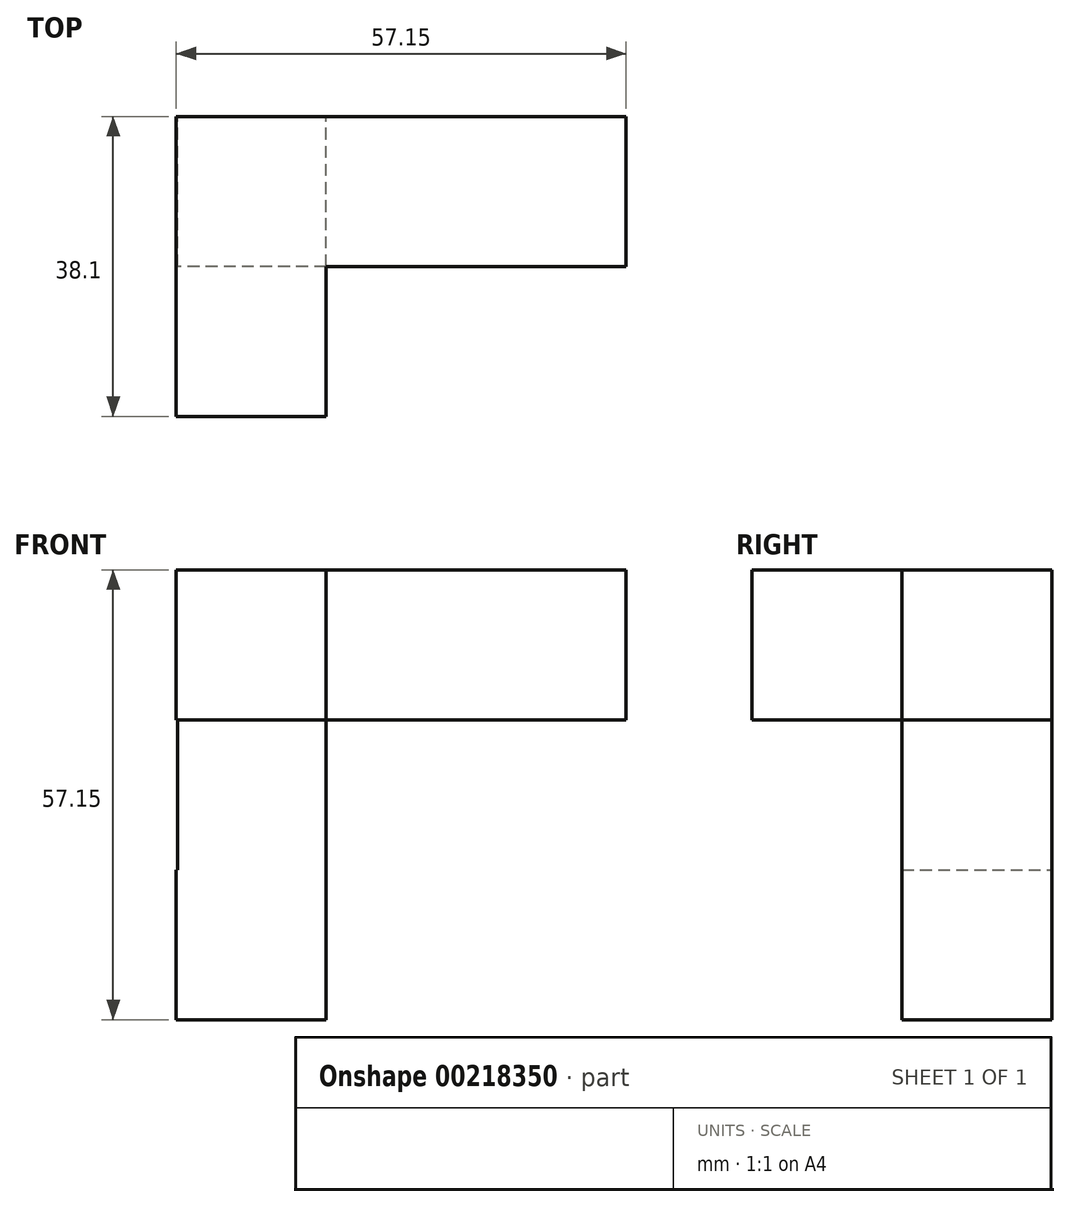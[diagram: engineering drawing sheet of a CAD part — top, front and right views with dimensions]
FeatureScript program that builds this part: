
annotation { "Feature Type Name" : "Feature", "Feature Type Description" : "" }
export const myFeature = defineFeature(function(context is Context, id is Id, definition is map)
    precondition{}
    {
        {
            var Q0;
            Q0=qCreatedBy(makeId("Front.planeOp"),FACE);
            var sketch = newSketch(context, id + "F0", { "sketchPlane" : qUnion([Q0])});
            skLineSegment(sketch, "E0.bottom", {"start": v(0, 0) * mm, "end": v(-19.05, 0) * mm});
            skLineSegment(sketch, "E0.top", {"start": v(0, 19.05) * mm, "end": v(-19.05, 19.05) * mm});
            skLineSegment(sketch, "E0.left", {"start": v(0, 0) * mm, "end": v(0, 19.05) * mm});
            skLineSegment(sketch, "E0.right", {"start": v(-19.05, 0) * mm, "end": v(-19.05, 19.05) * mm});
            skLineSegment(sketch, "E1.bottom", {"start": v(0, 0) * mm, "end": v(-18.85, 0) * mm});
            skLineSegment(sketch, "E1.top", {"start": v(0, -19.05) * mm, "end": v(-18.85, -19.05) * mm});
            skLineSegment(sketch, "E1.left", {"start": v(0, 0) * mm, "end": v(0, -19.05) * mm});
            skLineSegment(sketch, "E1.right", {"start": v(-18.85, 0) * mm, "end": v(-18.85, -19.05) * mm});
            skLineSegment(sketch, "E2.bottom", {"start": v(0, -19.05) * mm, "end": v(-19.05, -19.05) * mm});
            skLineSegment(sketch, "E2.top", {"start": v(0, -38.1) * mm, "end": v(-19.05, -38.1) * mm});
            skLineSegment(sketch, "E2.left", {"start": v(0, -19.05) * mm, "end": v(0, -38.1) * mm});
            skLineSegment(sketch, "E2.right", {"start": v(-19.05, -19.05) * mm, "end": v(-19.05, -38.1) * mm});
            skLineSegment(sketch, "E3.bottom", {"start": v(0, 19.05) * mm, "end": v(19.05, 19.05) * mm});
            skLineSegment(sketch, "E3.top", {"start": v(0, 0) * mm, "end": v(19.05, 0) * mm});
            skLineSegment(sketch, "E3.left", {"start": v(0, 19.05) * mm, "end": v(0, 0) * mm});
            skLineSegment(sketch, "E3.right", {"start": v(19.05, 19.05) * mm, "end": v(19.05, 0) * mm});
            skLineSegment(sketch, "E4.bottom", {"start": v(19.05, 19.05) * mm, "end": v(38.1, 19.05) * mm});
            skLineSegment(sketch, "E4.top", {"start": v(19.05, 0) * mm, "end": v(38.1, 0) * mm});
            skLineSegment(sketch, "E4.right", {"start": v(38.1, 19.05) * mm, "end": v(38.1, 0) * mm});
            skSolve(sketch);
        }
        {
            var Q0;
            Q0=makeQuery(id+"F0.imprint","IMPRINT",FACE,{"disambiguationData":[TD([[makeQuery(id+"F0.imprint","IMPRINT",EDGE,{"derivedFrom":sQuery(id+"F0.wireOp",EDGE,"E0.bottom")}),-1.0]])]});
            extrude(context, id + "F1", {"entities" : qUnion([Q0]), "depth" : 19.05 * mm});
        }
        {
            var Q0;
            Q0 = qSketchRegion(id + "F0", true);
            var Q1;
            Q1=makeQuery(id+"F1.opExtrude","CAP_FACE",FACE,{"disambiguationData":[OSD([sQuery(id+"F0.wireOp",EDGE,"E0.bottom"),sQuery(id+"F0.wireOp",EDGE,"E0.top"),sQuery(id+"F0.wireOp",EDGE,"E0.right"),sQuery(id+"F0.wireOp",EDGE,"E1.bottom"),sQuery(id+"F0.wireOp",EDGE,"E3.left")])],"isStart":false});
            extrude(context, id + "F2", {"entities" : qUnion([Q0, Q1]), "operationType" : NewBodyOperationType.ADD, "depth" : 19.05 * mm});
        }
    });
